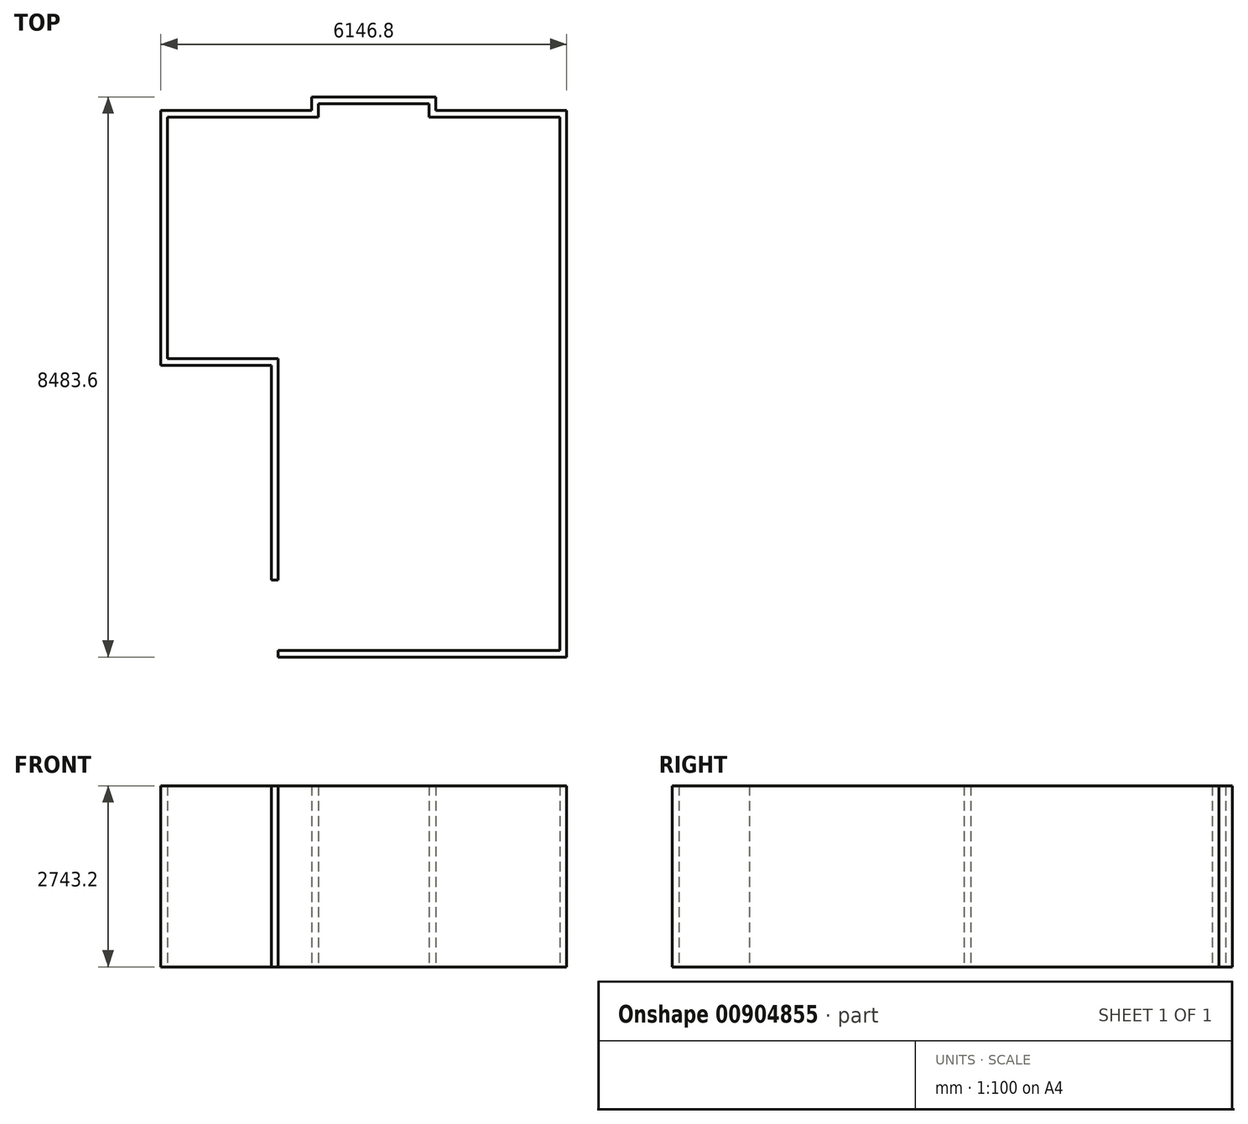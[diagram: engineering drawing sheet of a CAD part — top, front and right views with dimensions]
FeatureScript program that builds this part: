
annotation { "Feature Type Name" : "Feature", "Feature Type Description" : "" }
export const myFeature = defineFeature(function(context is Context, id is Id, definition is map)
    precondition{}
    {
        {
            var Q0;
            Q0=qCreatedBy(makeId("Top.planeOp"),FACE);
            var sketch = newSketch(context, id + "F0", { "sketchPlane" : qUnion([Q0])});
            skLineSegment(sketch, "E0", {"start": v(-3124.2, 381) * mm, "end": v(-3124.2, 4038.6) * mm});
            skLineSegment(sketch, "E1", {"start": v(-3124.2, 4038.6) * mm, "end": v(-838.2, 4038.6) * mm});
            skLineSegment(sketch, "E2", {"start": v(-838.2, 4038.6) * mm, "end": v(-838.2, 4241.8) * mm});
            skLineSegment(sketch, "E3", {"start": v(-838.2, 4241.8) * mm, "end": v(838.2, 4241.8) * mm});
            skLineSegment(sketch, "E4", {"start": v(838.2, 4241.8) * mm, "end": v(838.2, 4038.6) * mm});
            skLineSegment(sketch, "E5", {"start": v(838.2, 4038.6) * mm, "end": v(2819.4, 4038.6) * mm});
            skLineSegment(sketch, "E6", {"start": v(2819.4, 4038.6) * mm, "end": v(2819.4, -4038.6) * mm});
            skLineSegment(sketch, "E7", {"start": v(2819.4, -4038.6) * mm, "end": v(-1447.8, -4038.6) * mm});
            skLineSegment(sketch, "E8", {"start": v(-3124.2, 381) * mm, "end": v(-1447.8, 381) * mm});
            skLineSegment(sketch, "E9", {"start": v(-1447.8, 381) * mm, "end": v(-1447.8, -2971.8) * mm});
            skLineSegment(sketch, "E10.0", {"start": v(2921, -4140.2) * mm, "end": v(-1447.8, -4140.2) * mm});
            skLineSegment(sketch, "E10.1", {"start": v(2921, 4140.2) * mm, "end": v(2921, -4140.2) * mm});
            skLineSegment(sketch, "E10.2", {"start": v(939.8, 4140.2) * mm, "end": v(2921, 4140.2) * mm});
            skLineSegment(sketch, "E10.3", {"start": v(939.8, 4343.4) * mm, "end": v(939.8, 4140.2) * mm});
            skLineSegment(sketch, "E10.4", {"start": v(-939.8, 4343.4) * mm, "end": v(939.8, 4343.4) * mm});
            skLineSegment(sketch, "E10.5", {"start": v(-939.8, 4140.2) * mm, "end": v(-939.8, 4343.4) * mm});
            skLineSegment(sketch, "E10.6", {"start": v(-1549.4, 279.4) * mm, "end": v(-1549.4, -2971.8) * mm});
            skLineSegment(sketch, "E10.7", {"start": v(-3225.8, 279.4) * mm, "end": v(-1549.4, 279.4) * mm});
            skLineSegment(sketch, "E10.8", {"start": v(-3225.8, 279.4) * mm, "end": v(-3225.8, 4140.2) * mm});
            skLineSegment(sketch, "E10.9", {"start": v(-3225.8, 4140.2) * mm, "end": v(-939.8, 4140.2) * mm});
            skLineSegment(sketch, "E11", {"start": v(-1549.4, -2971.8) * mm, "end": v(-1447.8, -2971.8) * mm});
            skLineSegment(sketch, "E12", {"start": v(-1447.8, -4038.6) * mm, "end": v(-1447.8, -4140.2) * mm});
            skLineSegment(sketch, "E13", {"start": v(0, 0) * mm, "end": v(0, 4343.4) * mm, "construction": true});
            skPoint(sketch, "E13.endSnap0", {"position": v(0, 4343.4) * mm});
            skSolve(sketch);
        }
        {
            var Q0;
            Q0=makeQuery(id+"F0.imprint","IMPRINT",FACE,{"disambiguationData":[TD([[makeQuery(id+"F0.imprint","IMPRINT",EDGE,{"derivedFrom":sQuery(id+"F0.wireOp",EDGE,"E0")}),1.0]])]});
            extrude(context, id + "F1", {"entities" : qUnion([Q0]), "depth" : 2743.2 * mm, "offsetDistance" : 25.4 * mm});
        }
    });
